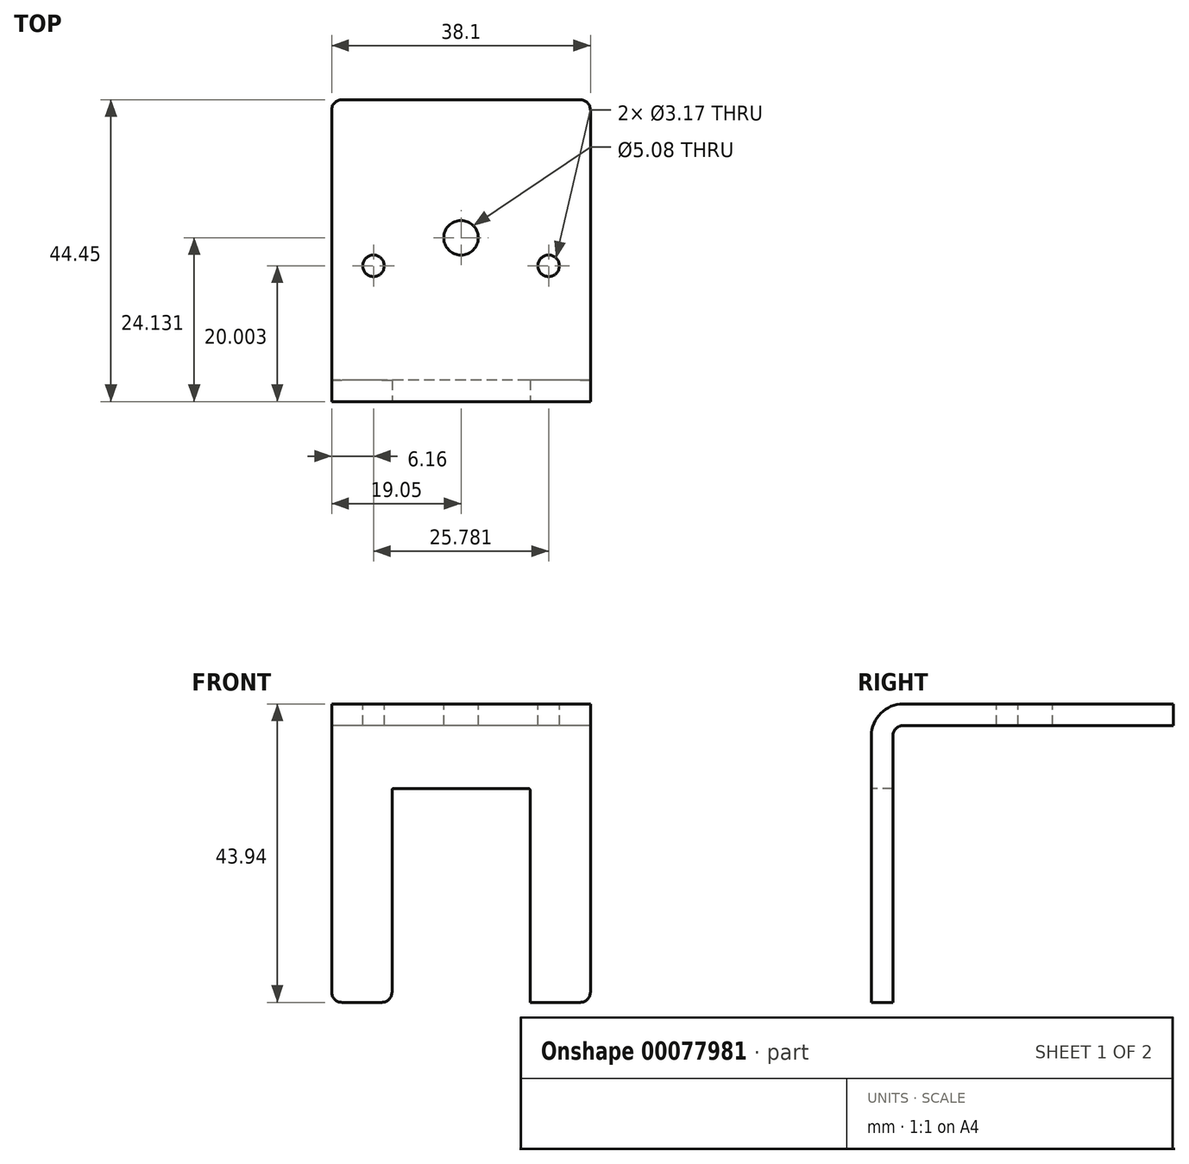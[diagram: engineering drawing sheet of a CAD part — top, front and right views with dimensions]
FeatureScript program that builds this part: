
annotation { "Feature Type Name" : "Feature", "Feature Type Description" : "" }
export const myFeature = defineFeature(function(context is Context, id is Id, definition is map)
    precondition{}
    {
        {
            var Q0;
            Q0=qCreatedBy(makeId("Right.planeOp"),FACE);
            var sketch = newSketch(context, id + "F0", { "sketchPlane" : qUnion([Q0])});
            skLineSegment(sketch, "E0.bottom", {"start": v(-60.85, 0) * mm, "end": v(-64.03, 0) * mm});
            skLineSegment(sketch, "E0.top", {"start": v(-0.53, 43.94) * mm, "end": v(-59.33, 43.94) * mm});
            skLineSegment(sketch, "E0.left", {"start": v(-0.53, 40.77) * mm, "end": v(-0.53, 43.94) * mm});
            skLineSegment(sketch, "E0.right", {"start": v(-64.03, 0) * mm, "end": v(-64.03, 39.24) * mm});
            skLineSegment(sketch, "E1", {"start": v(-60.85, 0) * mm, "end": v(-60.85, 39.24) * mm});
            skLineSegment(sketch, "E2", {"start": v(-59.33, 40.77) * mm, "end": v(-0.53, 40.77) * mm});
            skPoint(sketch, "E3.visualSharp", {"position": v(-60.85, 40.77) * mm});
            skArc(sketch, "E3.filletArc", {"start": v(-59.33, 40.77) * mm, "mid": v(-60.4, 40.32) * mm, "end": v(-60.85, 39.24) * mm});
            skPoint(sketch, "E4.visualSharp", {"position": v(-64.03, 43.94) * mm});
            skArc(sketch, "E4.filletArc", {"start": v(-59.33, 43.94) * mm, "mid": v(-62.65, 42.57) * mm, "end": v(-64.03, 39.24) * mm});
            skSolve(sketch);
        }
        {
            var Q0;
            Q0=qSketchRegion(id+"F0",true);
            extrude(context, id + "F1", {"entities" : qUnion([Q0]), "depth" : 38.1 * mm});
        }
        {
            var Q0;
            Q0=makeQuery(id+"F1.opExtrude","SWEPT_FACE",FACE,{"disambiguationData":[OSD([sQuery(id+"F0.wireOp",EDGE,"E0.right")])]});
            var sketch = newSketch(context, id + "F2", { "sketchPlane" : qUnion([Q0])});
            skLineSegment(sketch, "E5.bottom", {"start": v(8.9, 0) * mm, "end": v(29.21, 0) * mm});
            skLineSegment(sketch, "E5.top", {"start": v(9.14, 31.5) * mm, "end": v(28.96, 31.5) * mm});
            skLineSegment(sketch, "E5.left", {"start": v(8.9, 0) * mm, "end": v(8.9, 31.24) * mm});
            skLineSegment(sketch, "E5.right", {"start": v(29.21, 0) * mm, "end": v(29.21, 31.24) * mm});
            skPoint(sketch, "E6.visualSharp", {"position": v(8.9, 31.5) * mm});
            skArc(sketch, "E6.filletArc", {"start": v(9.14, 31.5) * mm, "mid": v(8.96, 31.42) * mm, "end": v(8.9, 31.24) * mm});
            skPoint(sketch, "E7.visualSharp", {"position": v(29.21, 31.5) * mm});
            skArc(sketch, "E7.filletArc", {"start": v(29.21, 31.24) * mm, "mid": v(29.14, 31.42) * mm, "end": v(28.96, 31.5) * mm});
            skSolve(sketch);
        }
        {
            var Q0;
            Q0=qSketchRegion(id+"F2",true);
            extrude(context, id + "F3", {"entities" : qUnion([Q0]), "operationType" : NewBodyOperationType.REMOVE, "endBound" : BoundingType.UP_TO_NEXT, "oppositeDirection" : true, "depth" : 25.4 * mm});
        }
        {
            var Q0;
            Q0=makeQuery(id+"F3.boolean.opBoolean","COPY",EDGE,{"derivedFrom":makeQuery(id+"F3.opExtrude","SWEPT_EDGE",EDGE,{"disambiguationData":[OSD([sQuery(id+"F0.wireOp",EDGE,"E0.bottom"),sQuery(id+"F0.wireOp",EDGE,"E0.right"),sQuery(id+"F2.wireOp",EDGE,"E5.bottom"),sQuery(id+"F2.wireOp",EDGE,"E5.left")])]})});
            var Q1;
            Q1=makeQuery(id+"F1.opExtrude","CAP_EDGE",EDGE,{"disambiguationData":[OSD([sQuery(id+"F0.wireOp",EDGE,"E0.bottom")])],"isStart":true});
            var Q2;
            Q2=makeQuery(id+"F3.boolean.opBoolean","COPY",EDGE,{"derivedFrom":makeQuery(id+"F3.opExtrude","SWEPT_EDGE",EDGE,{"disambiguationData":[OSD([sQuery(id+"F0.wireOp",EDGE,"E0.bottom"),sQuery(id+"F0.wireOp",EDGE,"E0.right"),sQuery(id+"F2.wireOp",EDGE,"E5.bottom"),sQuery(id+"F2.wireOp",EDGE,"E5.right")])]})});
            var Q3;
            Q3=makeQuery(id+"F1.opExtrude","CAP_EDGE",EDGE,{"disambiguationData":[OSD([sQuery(id+"F0.wireOp",EDGE,"E0.bottom")])],"isStart":false});
            var Q4;
            Q4=makeQuery(id+"F1.opExtrude","CAP_EDGE",EDGE,{"disambiguationData":[OSD([sQuery(id+"F0.wireOp",EDGE,"E0.left")])],"isStart":false});
            var Q5;
            Q5=makeQuery(id+"F1.opExtrude","CAP_EDGE",EDGE,{"disambiguationData":[OSD([sQuery(id+"F0.wireOp",EDGE,"E0.left")])],"isStart":true});
            fillet(context, id + "F4", {"entities" : qUnion([Q0, Q1, Q2, Q3, Q4, Q5]), "radius" : 1.52 * mm, "tangentPropagation" : true, "allowEdgeOverflow" : false});
        }
        {
            var Q0;
            Q0=makeQuery(id+"F1.opExtrude","SWEPT_FACE",FACE,{"disambiguationData":[OSD([sQuery(id+"F0.wireOp",EDGE,"E0.top")])]});
            var sketch = newSketch(context, id + "F5", { "sketchPlane" : qUnion([Q0])});
            skLineSegment(sketch, "E8", {"start": v(19.05, -0.53) * mm, "end": v(19.05, -59.33) * mm, "construction": true});
            skLineSegment(sketch, "E9", {"start": v(38.1, -44.03) * mm, "end": v(0, -44.03) * mm, "construction": true});
            skCircle(sketch, "E10", {"center": v(19.05, -8.15) * mm, "radius": 2.54 * mm});
            skCircle(sketch, "E11", {"center": v(19.05, -39.9) * mm, "radius": 2.54 * mm});
            skCircle(sketch, "E12", {"center": v(31.94, -44.03) * mm, "radius": 1.59 * mm});
            skCircle(sketch, "E13", {"center": v(6.16, -44.03) * mm, "radius": 1.59 * mm});
            skSolve(sketch);
        }
        {
            var Q0;
            Q0=qSketchRegion(id+"F5",true);
            extrude(context, id + "F6", {"entities" : qUnion([Q0]), "operationType" : NewBodyOperationType.REMOVE, "endBound" : BoundingType.UP_TO_NEXT, "oppositeDirection" : true, "depth" : 25.4 * mm});
        }
        {
            var Q0;
            Q0=makeQuery(id+"F1.opExtrude","SWEPT_FACE",FACE,{"disambiguationData":[OSD([sQuery(id+"F0.wireOp",EDGE,"E0.left")])]});
            var sketch = newSketch(context, id + "F7", { "sketchPlane" : qUnion([Q0])});
            skLineSegment(sketch, "E14.bottom", {"start": v(16.29, 19.52) * mm, "end": v(-54.66, 19.52) * mm});
            skLineSegment(sketch, "E14.top", {"start": v(16.29, 65.36) * mm, "end": v(-54.66, 65.36) * mm});
            skLineSegment(sketch, "E14.left", {"start": v(16.29, 19.52) * mm, "end": v(16.29, 65.36) * mm});
            skLineSegment(sketch, "E14.right", {"start": v(-54.66, 19.52) * mm, "end": v(-54.66, 65.36) * mm});
            skPoint(sketch, "E14.middle", {"position": v(-19.18, 42.44) * mm});
            skSolve(sketch);
        }
        {
            var Q0;
            Q0 = qSketchRegion(id + "F7", true);
            extrude(context, id + "F8", {"entities" : qUnion([Q0]), "operationType" : NewBodyOperationType.REMOVE, "oppositeDirection" : true, "depth" : 19.05 * mm});
        }
        {
            var Q0;
            Q0=makeQuery(id+"F8.boolean.opBoolean","INTERSECT",EDGE,{"derivedFrom":[makeQuery(id+"F1.opExtrude","CAP_FACE",FACE,{"disambiguationData":[OSD([sQuery(id+"F0.wireOp",EDGE,"E0.bottom"),sQuery(id+"F0.wireOp",EDGE,"E0.top"),sQuery(id+"F0.wireOp",EDGE,"E0.left"),sQuery(id+"F0.wireOp",EDGE,"E0.right"),sQuery(id+"F0.wireOp",EDGE,"E1"),sQuery(id+"F0.wireOp",EDGE,"E2"),sQuery(id+"F0.wireOp",EDGE,"E3.filletArc"),sQuery(id+"F0.wireOp",EDGE,"E4.filletArc")])],"isStart":false}),makeQuery(id+"F8.opExtrude","CAP_FACE",FACE,{"disambiguationData":[OSD([sQuery(id+"F7.wireOp",EDGE,"E14.bottom"),sQuery(id+"F7.wireOp",EDGE,"E14.top"),sQuery(id+"F7.wireOp",EDGE,"E14.left"),sQuery(id+"F7.wireOp",EDGE,"E14.right")])],"isStart":false})]});
            var Q1;
            Q1=makeQuery(id+"F8.boolean.opBoolean","INTERSECT",EDGE,{"derivedFrom":[makeQuery(id+"F1.opExtrude","CAP_FACE",FACE,{"disambiguationData":[OSD([sQuery(id+"F0.wireOp",EDGE,"E0.bottom"),sQuery(id+"F0.wireOp",EDGE,"E0.top"),sQuery(id+"F0.wireOp",EDGE,"E0.left"),sQuery(id+"F0.wireOp",EDGE,"E0.right"),sQuery(id+"F0.wireOp",EDGE,"E1"),sQuery(id+"F0.wireOp",EDGE,"E2"),sQuery(id+"F0.wireOp",EDGE,"E3.filletArc"),sQuery(id+"F0.wireOp",EDGE,"E4.filletArc")])],"isStart":true}),makeQuery(id+"F8.opExtrude","CAP_FACE",FACE,{"disambiguationData":[OSD([sQuery(id+"F7.wireOp",EDGE,"E14.bottom"),sQuery(id+"F7.wireOp",EDGE,"E14.top"),sQuery(id+"F7.wireOp",EDGE,"E14.left"),sQuery(id+"F7.wireOp",EDGE,"E14.right")])],"isStart":false})]});
            fillet(context, id + "F9", {"entities" : qUnion([Q0, Q1]), "radius" : 1.52 * mm, "tangentPropagation" : true, "allowEdgeOverflow" : false});
        }
    });
